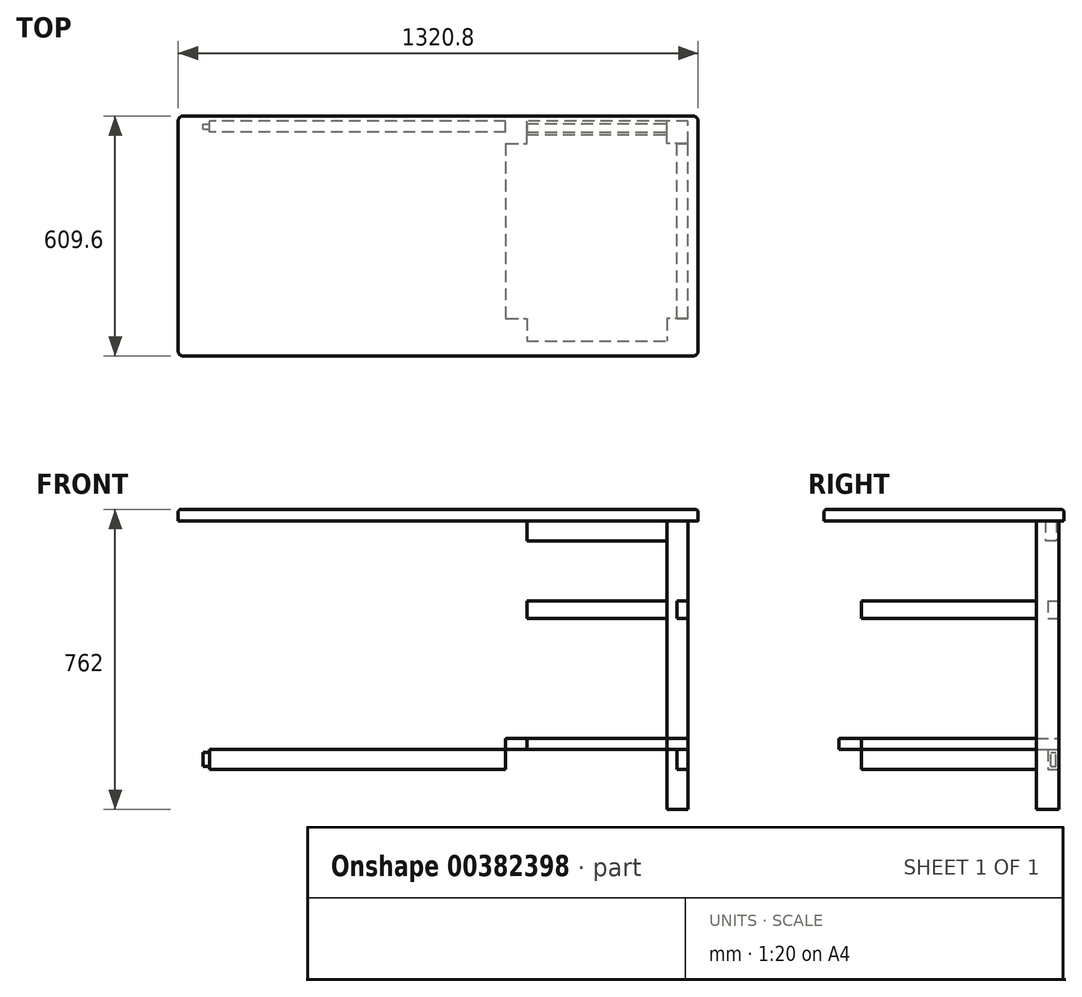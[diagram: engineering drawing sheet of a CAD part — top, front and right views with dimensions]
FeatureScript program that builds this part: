
annotation { "Feature Type Name" : "Feature", "Feature Type Description" : "" }
export const myFeature = defineFeature(function(context is Context, id is Id, definition is map)
    precondition{}
    {
        {
            var Q0;
            Q0=qCreatedBy(makeId("Front.planeOp"),FACE);
            var sketch = newSketch(context, id + "F0", { "sketchPlane" : qUnion([Q0])});
            skLineSegment(sketch, "E0.bottom", {"start": v(-635, 381) * mm, "end": v(635, 381) * mm});
            skLineSegment(sketch, "E0.top", {"start": v(-635, -381) * mm, "end": v(635, -381) * mm});
            skLineSegment(sketch, "E0.left", {"start": v(-635, 381) * mm, "end": v(-635, -381) * mm});
            skLineSegment(sketch, "E0.right", {"start": v(635, 381) * mm, "end": v(635, -381) * mm});
            skSolve(sketch);
        }
        {
            var Q0;
            Q0=qCreatedBy(makeId("Front.planeOp"),FACE);
            var sketch = newSketch(context, id + "F1", { "sketchPlane" : qUnion([Q0])});
            skLineSegment(sketch, "E1", {"start": v(-711.2, 352.43) * mm, "end": v(635, 352.43) * mm});
            skSolve(sketch);
        }
        {
            var Q0;
            Q0=qCreatedBy(makeId("Front.planeOp"),FACE);
            var sketch = newSketch(context, id + "F2", { "sketchPlane" : qUnion([Q0])});
            skLineSegment(sketch, "E2", {"start": v(-635, -279.4) * mm, "end": v(635, -279.4) * mm});
            skSolve(sketch);
        }
        {
            var Q0;
            Q0=sQuery(id+"F0.wireOp",EDGE,"E0.right");
            cPoint(context, id + "F3", {"entities" : qUnion([Q0]), "parameter" : 0.5});
        }
        {
            var Q0;
            Q0=qCreatedBy(makeId("Right.planeOp"),FACE);
            var Q1;
            Q1 = qCreatedBy(id + "F3" ,VERTEX);
            cPlane(context, id + "F4", {"entities" : qUnion([Q0, Q1]), "cplaneType" : CPlaneType.PLANE_POINT, "offset" : 25.4 * mm, "width" : 152.4 * mm, "height" : 152.4 * mm});
        }
        {
            var Q0;
            Q0=qCreatedBy(id+"F4.planeOp",FACE);
            var sketch = newSketch(context, id + "F5", { "sketchPlane" : qUnion([Q0])});
            skLineSegment(sketch, "E3.bottom", {"start": v(0, 381) * mm, "end": v(-584.2, 381) * mm});
            skLineSegment(sketch, "E3.top", {"start": v(0, -381) * mm, "end": v(-584.2, -381) * mm});
            skLineSegment(sketch, "E3.left", {"start": v(0, 381) * mm, "end": v(0, -381) * mm});
            skLineSegment(sketch, "E3.right", {"start": v(-584.2, 381) * mm, "end": v(-584.2, -381) * mm});
            skSolve(sketch);
        }
        {
            var Q0;
            Q0=qCreatedBy(id+"F4.planeOp",FACE);
            var sketch = newSketch(context, id + "F6", { "sketchPlane" : qUnion([Q0])});
            skLineSegment(sketch, "E4", {"start": v(0, -279.4) * mm, "end": v(-584.2, -279.4) * mm});
            skSolve(sketch);
        }
        {
            var Q0;
            Q0=qCreatedBy(makeId("Front.planeOp"),FACE);
            var sketch = newSketch(context, id + "F7", { "sketchPlane" : qUnion([Q0])});
            skLineSegment(sketch, "E5", {"start": v(-635, 301.63) * mm, "end": v(635, 301.63) * mm});
            skSolve(sketch);
        }
        {
            var Q0;
            Q0=qCreatedBy(id+"F4.planeOp",FACE);
            var sketch = newSketch(context, id + "F8", { "sketchPlane" : qUnion([Q0])});
            skLineSegment(sketch, "E6", {"start": v(0, 301.63) * mm, "end": v(-584.2, 301.62) * mm});
            skSolve(sketch);
        }
        {
            var Q0;
            Q0=qCreatedBy(makeId("Front.planeOp"),FACE);
            var sketch = newSketch(context, id + "F9", { "sketchPlane" : qUnion([Q0])});
            skLineSegment(sketch, "E7", {"start": v(-635, -228.6) * mm, "end": v(635, -228.6) * mm});
            skSolve(sketch);
        }
        {
            var Q0;
            Q0=qCreatedBy(id+"F4.planeOp",FACE);
            var sketch = newSketch(context, id + "F10", { "sketchPlane" : qUnion([Q0])});
            skLineSegment(sketch, "E8", {"start": v(0, 352.43) * mm, "end": v(-584.2, 352.42) * mm, "construction": true});
            skLineSegment(sketch, "E9.bottom", {"start": v(-12.7, 352.43) * mm, "end": v(-69.85, 352.43) * mm});
            skLineSegment(sketch, "E9.top", {"start": v(-12.7, -381) * mm, "end": v(-69.85, -381) * mm});
            skLineSegment(sketch, "E9.left", {"start": v(-12.7, 352.43) * mm, "end": v(-12.7, -381) * mm});
            skLineSegment(sketch, "E9.right", {"start": v(-69.85, 352.43) * mm, "end": v(-69.85, -381) * mm});
            skSolve(sketch);
        }
        {
            var Q0;
            Q0=qCreatedBy(makeId("Front.planeOp"),FACE);
            var Q1;
            Q1=sQuery(id+"F10.wireOp",VERTEX,"E9.left.start");
            cPlane(context, id + "F11", {"entities" : qUnion([Q0, Q1]), "cplaneType" : CPlaneType.PLANE_POINT, "offset" : 25.4 * mm, "width" : 152.4 * mm, "height" : 152.4 * mm});
        }
        {
            var Q0;
            Q0=qCreatedBy(makeId("Front.planeOp"),FACE);
            var sketch = newSketch(context, id + "F12", { "sketchPlane" : qUnion([Q0])});
            skLineSegment(sketch, "E10.bottom", {"start": v(635, 352.43) * mm, "end": v(581.02, 352.43) * mm});
            skLineSegment(sketch, "E10.top", {"start": v(635, -381) * mm, "end": v(581.03, -381) * mm});
            skLineSegment(sketch, "E10.left", {"start": v(635, 352.43) * mm, "end": v(635, -381) * mm});
            skLineSegment(sketch, "E10.right", {"start": v(581.02, 352.43) * mm, "end": v(581.03, -381) * mm});
            skLineSegment(sketch, "E11.MirrorCS", {"start": v(-635, 352.43) * mm, "end": v(-581.02, 352.43) * mm});
            skLineSegment(sketch, "E12.MirrorCS", {"start": v(-635, -381) * mm, "end": v(-581.03, -381) * mm});
            skLineSegment(sketch, "E13.MirrorCS", {"start": v(-581.02, 352.43) * mm, "end": v(-581.02, -381) * mm});
            skSolve(sketch);
        }
        {
            var Q0;
            Q0=qCreatedBy(id+"F11.planeOp",FACE);
            var sketch = newSketch(context, id + "F13", { "sketchPlane" : qUnion([Q0])});
            skLineSegment(sketch, "E14.bottom", {"start": v(635, 352.43) * mm, "end": v(581.02, 352.43) * mm});
            skLineSegment(sketch, "E14.top", {"start": v(635, -381) * mm, "end": v(581.03, -381) * mm});
            skLineSegment(sketch, "E14.left", {"start": v(635, 352.43) * mm, "end": v(635, -381) * mm});
            skLineSegment(sketch, "E14.right", {"start": v(581.02, 352.43) * mm, "end": v(581.03, -381) * mm});
            skSolve(sketch);
        }
        {
            var Q0;
            Q0=qCreatedBy(makeId("Front.planeOp"),FACE);
            var sketch = newSketch(context, id + "F14", { "sketchPlane" : qUnion([Q0])});
            skLineSegment(sketch, "E15.bottom", {"start": v(171.45, 352.43) * mm, "end": v(225.42, 352.43) * mm});
            skLineSegment(sketch, "E15.top", {"start": v(171.45, -381) * mm, "end": v(225.43, -381) * mm});
            skLineSegment(sketch, "E15.left", {"start": v(171.45, 352.43) * mm, "end": v(171.45, -381) * mm});
            skLineSegment(sketch, "E15.right", {"start": v(225.42, 352.43) * mm, "end": v(225.43, -381) * mm});
            skSolve(sketch);
        }
        {
            var Q0;
            Q0=makeQuery(id+"F13.imprint","IMPRINT",FACE,{"disambiguationData":[TD([[makeQuery(id+"F13.imprint","IMPRINT",EDGE,{"derivedFrom":sQuery(id+"F13.wireOp",EDGE,"E14.bottom")}),1.0]])]});
            var Q1;
            Q1=sQuery(id+"F10.wireOp",VERTEX,"E9.right.start");
            extrude(context, id + "F15", {"entities" : qUnion([Q0]), "endBound" : BoundingType.UP_TO_VERTEX, "endBoundEntityVertex" : qUnion([Q1]), "depth" : 76.2 * mm});
        }
        {
            var Q0;
            Q0=makeQuery(id+"F15.opExtrude","SWEPT_FACE",FACE,{"disambiguationData":[OSD([sQuery(id+"F13.wireOp",EDGE,"E14.right")])]});
            var sketch = newSketch(context, id + "F16", { "sketchPlane" : qUnion([Q0])});
            skLineSegment(sketch, "E16.bottom", {"start": v(19.05, 352.42) * mm, "end": v(47.62, 352.42) * mm});
            skLineSegment(sketch, "E16.top", {"start": v(19.05, 301.62) * mm, "end": v(47.62, 301.62) * mm});
            skLineSegment(sketch, "E16.left", {"start": v(19.05, 352.42) * mm, "end": v(19.05, 301.62) * mm});
            skLineSegment(sketch, "E16.right", {"start": v(47.62, 352.42) * mm, "end": v(47.62, 301.62) * mm});
            skSolve(sketch);
        }
        {
            var Q0;
            Q0 = qSketchRegion(id + "F16", true);
            var Q1;
            Q1=sQuery(id+"F14.wireOp",VERTEX,"E15.right.start");
            extrude(context, id + "F17", {"entities" : qUnion([Q0]), "endBound" : BoundingType.UP_TO_VERTEX, "endBoundEntityVertex" : qUnion([Q1]), "depth" : 25.4 * mm});
        }
        {
            var Q0;
            Q0=qCreatedBy(id+"F4.planeOp",FACE);
            var sketch = newSketch(context, id + "F18", { "sketchPlane" : qUnion([Q0])});
            skLineSegment(sketch, "E17.bottom", {"start": v(-571.5, 352.42) * mm, "end": v(-514.35, 352.42) * mm});
            skLineSegment(sketch, "E17.top", {"start": v(-571.5, -381) * mm, "end": v(-514.35, -381) * mm});
            skLineSegment(sketch, "E17.left", {"start": v(-571.5, 352.42) * mm, "end": v(-571.5, -381) * mm});
            skLineSegment(sketch, "E17.right", {"start": v(-514.35, 352.42) * mm, "end": v(-514.35, -381) * mm});
            skLineSegment(sketch, "E18", {"start": v(0, 352.43) * mm, "end": v(-12.7, 352.43) * mm, "construction": true});
            skLineSegment(sketch, "E19", {"start": v(-571.5, 352.42) * mm, "end": v(-584.2, 352.42) * mm, "construction": true});
            skSolve(sketch);
        }
        {
            var Q0;
            Q0=qCreatedBy(id+"F4.planeOp",FACE);
            var sketch = newSketch(context, id + "F19", { "sketchPlane" : qUnion([Q0])});
            skLineSegment(sketch, "E20.bottom", {"start": v(-514.35, -228.6) * mm, "end": v(-69.85, -228.6) * mm});
            skLineSegment(sketch, "E20.top", {"start": v(-514.35, -279.4) * mm, "end": v(-69.85, -279.4) * mm});
            skLineSegment(sketch, "E20.left", {"start": v(-514.35, -228.6) * mm, "end": v(-514.35, -279.4) * mm});
            skLineSegment(sketch, "E20.right", {"start": v(-69.85, -228.6) * mm, "end": v(-69.85, -279.4) * mm});
            skLineSegment(sketch, "E21", {"start": v(0, -228.6) * mm, "end": v(-584.2, -228.6) * mm, "construction": true});
            skSolve(sketch);
        }
        {
            var Q0;
            Q0=qCreatedBy(id+"F11.planeOp",FACE);
            var sketch = newSketch(context, id + "F20", { "sketchPlane" : qUnion([Q0])});
            skLineSegment(sketch, "E22.bottom", {"start": v(171.45, -228.6) * mm, "end": v(-581.02, -228.6) * mm});
            skLineSegment(sketch, "E22.top", {"start": v(171.45, -279.4) * mm, "end": v(-581.02, -279.4) * mm});
            skLineSegment(sketch, "E22.left", {"start": v(171.45, -228.6) * mm, "end": v(171.45, -279.4) * mm});
            skLineSegment(sketch, "E22.right", {"start": v(-581.02, -228.6) * mm, "end": v(-581.02, -279.4) * mm});
            skSolve(sketch);
        }
        {
            var Q0;
            Q0 = qSketchRegion(id + "F20", true);
            var Q1;
            Q1=sQuery(id+"F16.wireOp",VERTEX,"E16.right.end");
            extrude(context, id + "F21", {"entities" : qUnion([Q0]), "endBoundEntityVertex" : qUnion([Q1]), "depth" : 28.57 * mm});
        }
        {
            var Q0;
            Q0=qCreatedBy(makeId("Front.planeOp"),FACE);
            var sketch = newSketch(context, id + "F22", { "sketchPlane" : qUnion([Q0])});
            skPoint(sketch, "E23.orphan", {"position": v(-635, -381) * mm});
            skPoint(sketch, "E24.orphan", {"position": v(635, -381) * mm});
            skPoint(sketch, "E25.0.start.orphan", {"position": v(635, 381) * mm});
            skPoint(sketch, "E26.0.end.orphan", {"position": v(635, 352.43) * mm});
            skPoint(sketch, "E26.0.start.orphan", {"position": v(-711.2, 352.43) * mm});
            skPoint(sketch, "E27.0.start.orphan", {"position": v(-635, 381) * mm});
            skLineSegment(sketch, "E28.bottom", {"start": v(-660.4, 352.43) * mm, "end": v(660.4, 352.43) * mm});
            skLineSegment(sketch, "E28.top", {"start": v(-660.4, 381) * mm, "end": v(660.4, 381) * mm});
            skLineSegment(sketch, "E28.left", {"start": v(-660.4, 381) * mm, "end": v(-660.4, 352.43) * mm});
            skLineSegment(sketch, "E28.right", {"start": v(660.4, 381) * mm, "end": v(660.4, 352.43) * mm});
            skSolve(sketch);
        }
        {
            var Q0;
            Q0 = qSketchRegion(id + "F19", true);
            extrude(context, id + "F23", {"entities" : qUnion([Q0]), "oppositeDirection" : true, "depth" : 28.57 * mm});
        }
        {
            var Q0;
            Q0 = qSketchRegion(id + "F22", true);
            var Q1;
            Q1=sQuery(id+"F8.wireOp",VERTEX,"E6.end");
            extrude(context, id + "F24", {"entities" : qUnion([Q0]), "endBoundEntityVertex" : qUnion([Q1]), "depth" : 609.6 * mm});
        }
        {
            var Q0;
            Q0=makeQuery(id+"F24.opExtrude","CAP_EDGE",EDGE,{"disambiguationData":[OSD([sQuery(id+"F22.wireOp",EDGE,"E28.right")])],"isStart":false});
            var Q1;
            Q1=makeQuery(id+"F24.opExtrude","CAP_EDGE",EDGE,{"disambiguationData":[OSD([sQuery(id+"F22.wireOp",EDGE,"E28.right")])],"isStart":true});
            var Q2;
            Q2=makeQuery(id+"F24.opExtrude","CAP_EDGE",EDGE,{"disambiguationData":[OSD([sQuery(id+"F22.wireOp",EDGE,"E28.left")])],"isStart":true});
            var Q3;
            Q3=makeQuery(id+"F24.opExtrude","CAP_EDGE",EDGE,{"disambiguationData":[OSD([sQuery(id+"F22.wireOp",EDGE,"E28.left")])],"isStart":false});
            fillet(context, id + "F25", {"entities" : qUnion([Q0, Q1, Q2, Q3]), "radius" : 12.7 * mm, "tangentPropagation" : true, "allowEdgeOverflow" : false});
        }
        {
            var Q0;
            Q0=makeQuery(id+"F24.opExtrude","SWEPT_EDGE",EDGE,{"disambiguationData":[OSD([sQuery(id+"F22.wireOp",EDGE,"E28.top"),sQuery(id+"F22.wireOp",EDGE,"E28.left")])]});
            fillet(context, id + "F26", {"entities" : qUnion([Q0]), "radius" : 6.35 * mm, "tangentPropagation" : true, "allowEdgeOverflow" : false});
        }
        {
            var Q0;
            Q0=makeQuery(id+"F23.opExtrude","SWEPT_FACE",FACE,{"disambiguationData":[OSD([sQuery(id+"F19.wireOp",EDGE,"E20.bottom")])]});
            var sketch = newSketch(context, id + "F27", { "sketchPlane" : qUnion([Q0])});
            skLineSegment(sketch, "E29", {"start": v(581.03, 0) * mm, "end": v(225.42, 0) * mm, "construction": true});
            skPoint(sketch, "E30", {"position": v(403.23, 0) * mm});
            skLineSegment(sketch, "E31", {"start": v(403.23, 0) * mm, "end": v(403.23, -571.5) * mm, "construction": true});
            skLineSegment(sketch, "E32", {"start": v(581.03, -69.85) * mm, "end": v(581.03, -12.7) * mm});
            skLineSegment(sketch, "E33", {"start": v(581.03, -12.7) * mm, "end": v(403.23, -12.7) * mm});
            skPoint(sketch, "E34", {"position": v(606.42, -292.1) * mm});
            skLineSegment(sketch, "E35", {"start": v(606.42, -292.1) * mm, "end": v(403.23, -292.1) * mm, "construction": true});
            skLineSegment(sketch, "E36.MirrorCS", {"start": v(635, -514.35) * mm, "end": v(581.03, -514.35) * mm});
            skLineSegment(sketch, "E37.MirrorCS", {"start": v(581.03, -571.5) * mm, "end": v(403.23, -571.5) * mm});
            skLineSegment(sketch, "E38.MirrorCS", {"start": v(581.03, -514.35) * mm, "end": v(581.03, -571.5) * mm});
            skLineSegment(sketch, "E39", {"start": v(635, -69.85) * mm, "end": v(635, -514.35) * mm});
            skLineSegment(sketch, "E40.MirrorCS", {"start": v(225.42, -571.5) * mm, "end": v(403.23, -571.5) * mm});
            skLineSegment(sketch, "E41.MirrorCS", {"start": v(225.42, -514.35) * mm, "end": v(225.42, -571.5) * mm});
            skLineSegment(sketch, "E42.MirrorCS", {"start": v(171.45, -514.35) * mm, "end": v(225.43, -514.35) * mm});
            skLineSegment(sketch, "E43.MirrorCS", {"start": v(171.45, -69.85) * mm, "end": v(171.45, -514.35) * mm});
            skLineSegment(sketch, "E44.MirrorCS", {"start": v(171.45, -69.85) * mm, "end": v(225.42, -69.85) * mm});
            skLineSegment(sketch, "E45.MirrorCS", {"start": v(225.42, -12.7) * mm, "end": v(403.23, -12.7) * mm});
            skLineSegment(sketch, "E46.MirrorCS", {"start": v(225.42, -69.85) * mm, "end": v(225.42, -12.7) * mm});
            skLineSegment(sketch, "E47.MirrorCS", {"start": v(635, -69.85) * mm, "end": v(581.03, -69.85) * mm});
            skSolve(sketch);
        }
        {
            var Q0;
            {var subQ3=sQuery(id+"F27.wireOp",EDGE,"E32");Q0=makeQuery(id+"F27.imprint","IMPRINT",FACE,{"disambiguationData":[TD([[makeQuery(id+"F27.imprint","IMPRINT",EDGE,{"derivedFrom":subQ3}),1.0]])]});}
            var Q1;
            {var subQ0=sQuery(id+"F27.wireOp",EDGE,"E39");Q1=makeQuery(id+"F27.imprint","IMPRINT",FACE,{"disambiguationData":[TD([[makeQuery(id+"F27.imprint","IMPRINT",EDGE,{"derivedFrom":subQ0}),1.0]])]});}
            extrude(context, id + "F28", {"entities" : qUnion([Q0, Q1]), "depth" : 28.57 * mm});
        }
        {
            var Q0;
            Q0=makeQuery(id+"F28.opExtrude","CAP_EDGE",EDGE,{"disambiguationData":[OSD([sQuery(id+"F27.wireOp",EDGE,"E37.MirrorCS"),sQuery(id+"F27.wireOp",EDGE,"E40.MirrorCS")])],"isStart":false});
            var Q1;
            Q1=makeQuery(id+"F28.opExtrude","CAP_EDGE",EDGE,{"disambiguationData":[OSD([sQuery(id+"F27.wireOp",EDGE,"E39")])],"isStart":false});
            var Q2;
            Q2=makeQuery(id+"F28.opExtrude","CAP_EDGE",EDGE,{"disambiguationData":[OSD([sQuery(id+"F27.wireOp",EDGE,"E33"),sQuery(id+"F27.wireOp",EDGE,"E45.MirrorCS")])],"isStart":false});
            var Q3;
            Q3=makeQuery(id+"F28.opExtrude","CAP_EDGE",EDGE,{"disambiguationData":[OSD([sQuery(id+"F27.wireOp",EDGE,"E43.MirrorCS")])],"isStart":false});
            fillet(context, id + "F29", {"entities" : qUnion([Q0, Q1, Q2, Q3]), "radius" : 3.17 * mm, "tangentPropagation" : true, "allowEdgeOverflow" : false});
        }
        {
            var Q0;
            Q0=qCreatedBy(id+"F4.planeOp",FACE);
            var sketch = newSketch(context, id + "F30", { "sketchPlane" : qUnion([Q0])});
            skLineSegment(sketch, "E48.bottom", {"start": v(-514.35, 149.22) * mm, "end": v(-69.85, 149.22) * mm});
            skLineSegment(sketch, "E48.top", {"start": v(-514.35, 104.77) * mm, "end": v(-69.85, 104.77) * mm});
            skLineSegment(sketch, "E48.left", {"start": v(-514.35, 149.22) * mm, "end": v(-514.35, 104.77) * mm});
            skLineSegment(sketch, "E48.right", {"start": v(-69.85, 149.22) * mm, "end": v(-69.85, 104.77) * mm});
            skLineSegment(sketch, "E49.top", {"start": v(-514.35, 177.8) * mm, "end": v(-69.85, 177.8) * mm, "construction": true});
            skLineSegment(sketch, "E49.left", {"start": v(-514.35, 149.22) * mm, "end": v(-514.35, 177.8) * mm, "construction": true});
            skLineSegment(sketch, "E49.right", {"start": v(-69.85, 149.22) * mm, "end": v(-69.85, 177.8) * mm, "construction": true});
            skSolve(sketch);
        }
        {
            var Q0;
            Q0=makeQuery(id+"F30.imprint","IMPRINT",FACE,{"disambiguationData":[TD([[makeQuery(id+"F30.imprint","IMPRINT",EDGE,{"derivedFrom":sQuery(id+"F30.wireOp",EDGE,"E48.bottom")}),-1.0]])]});
            extrude(context, id + "F31", {"entities" : qUnion([Q0]), "oppositeDirection" : true, "depth" : 28.57 * mm});
        }
        {
            var Q0;
            Q0=qCreatedBy(id+"F11.planeOp",FACE);
            var sketch = newSketch(context, id + "F32", { "sketchPlane" : qUnion([Q0])});
            skLineSegment(sketch, "E50", {"start": v(683.56, 149.22) * mm, "end": v(225.42, 149.22) * mm, "construction": true});
            skLineSegment(sketch, "E51.bottom", {"start": v(225.42, 149.22) * mm, "end": v(581.02, 149.22) * mm});
            skLineSegment(sketch, "E51.top", {"start": v(225.42, 104.77) * mm, "end": v(581.02, 104.77) * mm});
            skLineSegment(sketch, "E51.left", {"start": v(225.42, 149.22) * mm, "end": v(225.42, 104.77) * mm});
            skLineSegment(sketch, "E51.right", {"start": v(581.02, 149.22) * mm, "end": v(581.02, 104.77) * mm});
            skSolve(sketch);
        }
        {
            var Q0;
            Q0=makeQuery(id+"F32.imprint","IMPRINT",FACE,{"disambiguationData":[TD([[makeQuery(id+"F32.imprint","IMPRINT",EDGE,{"derivedFrom":sQuery(id+"F32.wireOp",EDGE,"E51.bottom")}),-1.0]])]});
            extrude(context, id + "F33", {"entities" : qUnion([Q0]), "depth" : 28.57 * mm});
        }
        {
            var Q0;
            Q0=makeQuery(id+"F21.opExtrude","SWEPT_FACE",FACE,{"disambiguationData":[OSD([sQuery(id+"F20.wireOp",EDGE,"E22.right")])]});
            var sketch = newSketch(context, id + "F34", { "sketchPlane" : qUnion([Q0])});
            skPoint(sketch, "E52", {"position": v(26.99, -228.6) * mm});
            skLineSegment(sketch, "E53", {"start": v(26.99, -228.6) * mm, "end": v(26.99, -279.4) * mm, "construction": true});
            skPoint(sketch, "E54", {"position": v(26.99, -254) * mm});
            skLineSegment(sketch, "E55.bottom", {"start": v(33.34, -271.46) * mm, "end": v(20.64, -271.46) * mm});
            skLineSegment(sketch, "E55.top", {"start": v(33.34, -236.54) * mm, "end": v(20.64, -236.54) * mm});
            skLineSegment(sketch, "E55.left", {"start": v(33.34, -271.46) * mm, "end": v(33.34, -236.54) * mm});
            skLineSegment(sketch, "E55.right", {"start": v(20.64, -271.46) * mm, "end": v(20.64, -236.54) * mm});
            skLineSegment(sketch, "E56", {"start": v(33.34, -236.54) * mm, "end": v(33.34, -228.6) * mm, "construction": true});
            skLineSegment(sketch, "E57", {"start": v(33.34, -271.46) * mm, "end": v(41.28, -271.46) * mm, "construction": true});
            skSolve(sketch);
        }
        {
            var Q0;
            Q0=makeQuery(id+"F34.imprint","IMPRINT",FACE,{"disambiguationData":[TD([[makeQuery(id+"F34.imprint","IMPRINT",EDGE,{"derivedFrom":sQuery(id+"F34.wireOp",EDGE,"E55.bottom")}),-1.0]])]});
            extrude(context, id + "F35", {"entities" : qUnion([Q0]), "operationType" : NewBodyOperationType.ADD, "depth" : 15.88 * mm, "offsetDistance" : 25.4 * mm});
        }
    });
